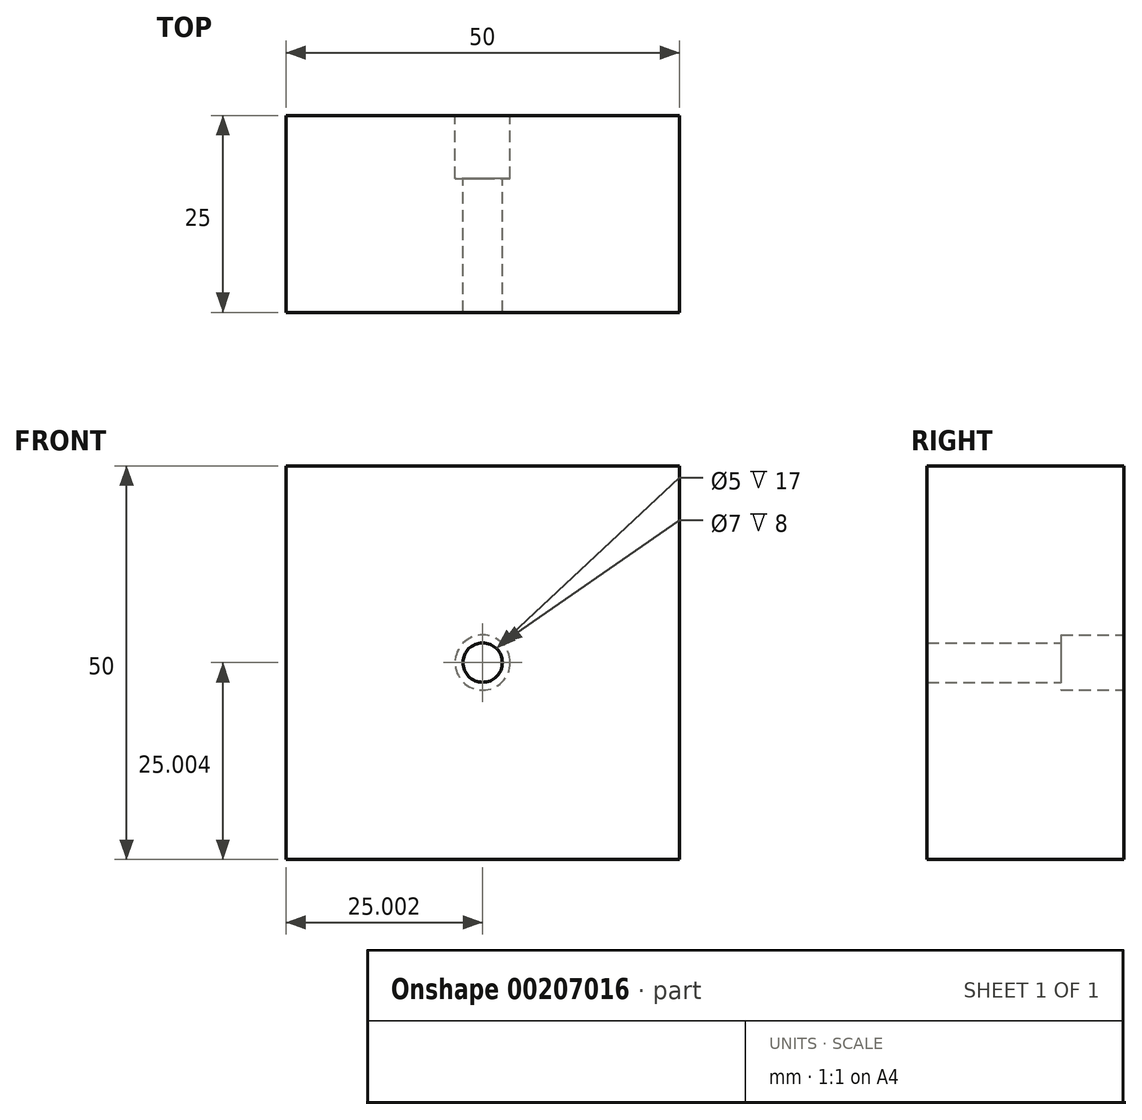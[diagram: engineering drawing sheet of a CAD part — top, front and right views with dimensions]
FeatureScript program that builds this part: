
annotation { "Feature Type Name" : "Feature", "Feature Type Description" : "" }
export const myFeature = defineFeature(function(context is Context, id is Id, definition is map)
    precondition{}
    {
        {
            var Q0;
            Q0=qCreatedBy(makeId("Front.planeOp"),FACE);
            var sketch = newSketch(context, id + "F0", { "sketchPlane" : qUnion([Q0])});
            skLineSegment(sketch, "E0.bottom", {"start": v(-109.82, 18.75) * mm, "end": v(-159.82, 18.75) * mm});
            skLineSegment(sketch, "E0.top", {"start": v(-109.82, 68.75) * mm, "end": v(-159.82, 68.75) * mm});
            skLineSegment(sketch, "E0.left", {"start": v(-109.82, 18.75) * mm, "end": v(-109.82, 68.75) * mm});
            skLineSegment(sketch, "E0.right", {"start": v(-159.82, 18.75) * mm, "end": v(-159.82, 68.75) * mm});
            skPoint(sketch, "E0.middle", {"position": v(-134.82, 43.75) * mm});
            skSolve(sketch);
        }
        {
            var Q0;
            Q0 = qSketchRegion(id + "F0", true);
            extrude(context, id + "F1", {"entities" : qUnion([Q0]), "depth" : 25 * mm});
        }
        {
            assignVariable(context, id + "F2", {"name" : "x", "anyValue" : 5});
        }
        {
            var Q0;
            Q0=sQuery(id+"F0.wireOp",VERTEX,"E0.middle");
            var Q1;
            Q1=makeQuery(id+"F1.opExtrude","SWEPT_BODY",BODY,{"disambiguationData":[OSD([sQuery(id+"F0.wireOp",EDGE,"E0.bottom"),sQuery(id+"F0.wireOp",EDGE,"E0.top"),sQuery(id+"F0.wireOp",EDGE,"E0.left"),sQuery(id+"F0.wireOp",EDGE,"E0.right")])]});
            hole(context, id + "F3", {"style" : HoleStyle.C_BORE, "endStyle" : HoleEndStyle.BLIND, "oppositeDirection" : true, "holeDiameter" : (getVariable(context, 'x')) * mm, "cBoreDiameter" : (getVariable(context, 'x') + 2) * mm, "cBoreDepth" : (getVariable(context, 'x') + 3) * mm, "holeDepth" : (getVariable(context, 'x') * 5) * mm, "startFromSketch" : true, "locations" : qUnion([Q0]), "scope" : qUnion([Q1])});
        }
    });
